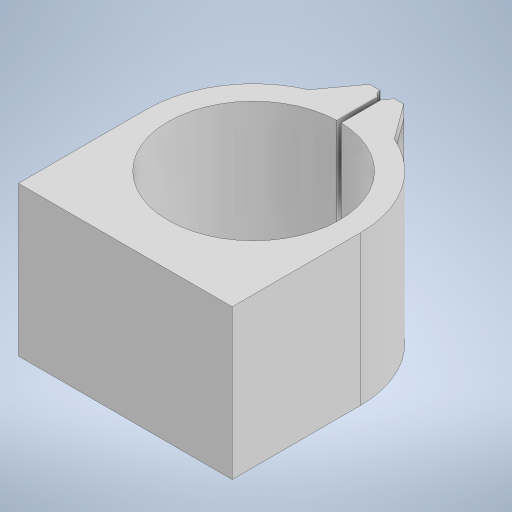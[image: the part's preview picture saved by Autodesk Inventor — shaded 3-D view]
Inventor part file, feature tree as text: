
AUTODESK INVENTOR PART (.ipt)
format: ipt  version: 2024 (Build 280153000, 153)  size: 247,808 bytes
history: native  units: mm
features: extrude x5, sketch x5, projected_geometry x1
ambient origin geometry x8: Origin, YZ Plane, XZ Plane, XY Plane, X Axis, Y Axis, Z Axis, Center Point
bodies: Solid1 (feature_tree)
feature tree (11):
  extrude  "Extrusion1"  Depth=70.0mm TaperAngle=0.0deg
  extrude  "Extrusion2"  TaperAngle=0.0deg  [1 undecoded]
  extrude  "Extrusion3"  Depth=6.1mm
  extrude  "Extrusion4"  [1 undecoded]
  extrude  "Extrusion5"  [1 undecoded]
  sketch  "Sketch1"  dims[d0=100.0mm d1=70.0mm d2=0.0mm]
  sketch  "Sketch2"  dims[d3=100.0mm d4=0.0mm d5=0.0mm d6=0.0mm]
  sketch  "Sketch3"  dims[d7=6.0mm d8=0.0mm d9=6.1mm]
  sketch  "Sketch4"  dims[d10=10.0mm d11=0.0mm]
  sketch  "Sketch5"
  projected_geometry  "Projected Loop1"
note: 3 required parameter values undecoded (feature->parameter linkage not recoverable at this tier; creation-order binding heuristic only, values carry confidence <= 0.55)
